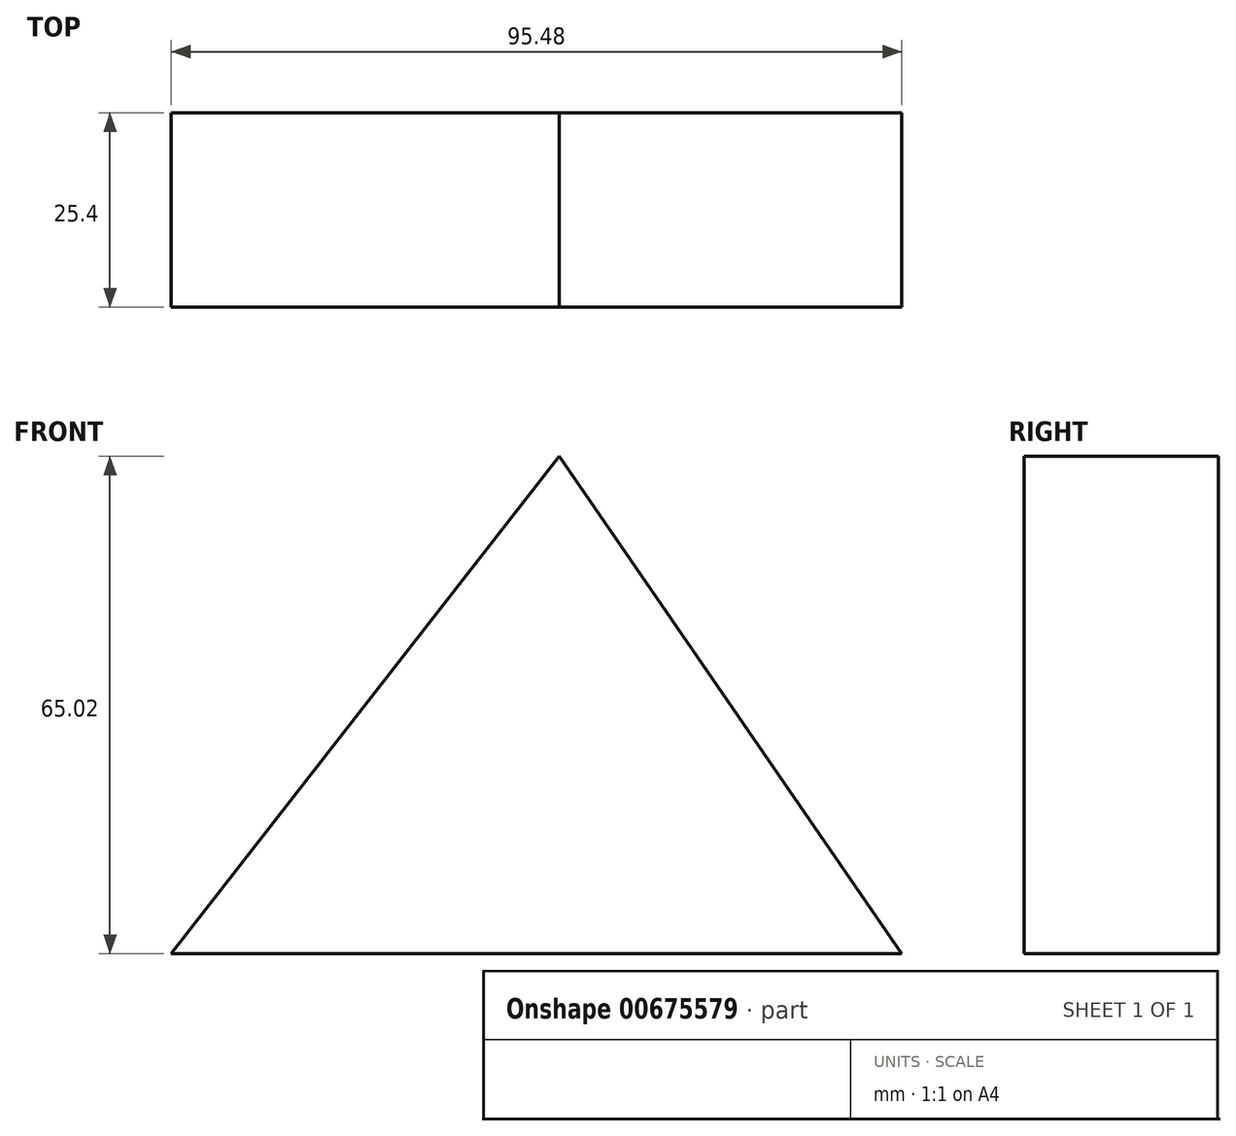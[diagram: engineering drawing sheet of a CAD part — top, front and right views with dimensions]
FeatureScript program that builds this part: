
annotation { "Feature Type Name" : "Feature", "Feature Type Description" : "" }
export const myFeature = defineFeature(function(context is Context, id is Id, definition is map)
    precondition{}
    {
        {
            var Q0;
            Q0=qCreatedBy(makeId("Front.planeOp"),FACE);
            var sketch = newSketch(context, id + "F0", { "sketchPlane" : qUnion([Q0])});
            skLineSegment(sketch, "E0", {"start": v(-50.7, 0) * mm, "end": v(0, 65.02) * mm});
            skLineSegment(sketch, "E1", {"start": v(0, 65.02) * mm, "end": v(44.78, 0) * mm});
            skLineSegment(sketch, "E2", {"start": v(44.78, 0) * mm, "end": v(-50.7, 0) * mm});
            skSolve(sketch);
        }
        {
            var Q0;
            Q0 = qSketchRegion(id + "F0", true);
            extrude(context, id + "F1", {"entities" : qUnion([Q0]), "depth" : 25.4 * mm, "offsetDistance" : 25.4 * mm});
        }
    });
